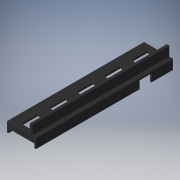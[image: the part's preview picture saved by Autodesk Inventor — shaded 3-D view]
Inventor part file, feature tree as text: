
AUTODESK INVENTOR PART (.ipt)
format: ipt  version: 2019 (Build 230136000, 136)  size: 193,024 bytes
history: native  units: mm
features: other x56, extrude x8, sketch x8
ambient origin geometry x8: Origin, YZ Plane, XZ Plane, XY Plane, X Axis, Y Axis, Z Axis, Center Point
bodies: Solid1 (feature_tree)
feature tree (72):
  extrude  "Extrusion1"  Depth=178.0mm TaperAngle=0.0deg
  extrude  "Extrusion2"  Depth=8.0mm TaperAngle=0.0deg
  extrude  "Extrusion3"  Depth=8.0mm TaperAngle=0.0deg
  extrude  "Extrusion4"  Depth=4.7mm TaperAngle=0.0deg
  extrude  "Extrusion5"  [1 undecoded]
  extrude  "Extrusion6"  [1 undecoded]
  extrude  "Extrusion7"  [1 undecoded]
  extrude  "Extrusion8"  [1 undecoded]
  other  "p_XY"
  other  "p_YZ"
  other  "p_ZX"
  other  "p_X"
  other  "p_Y"
  other  "p_Z"
  other  "p_Center"
  other  "p1_XY"
  other  "p1_YZ"
  other  "p1_ZX"
  other  "p1_X"
  other  "p1_Y"
  other  "p1_Z"
  other  "p1_Center"
  other  "p2_XY"
  other  "p2_YZ"
  other  "p2_ZX"
  other  "p2_X"
  other  "p2_Y"
  other  "p2_Z"
  other  "p2_Center"
  other  "p3_XY"
  other  "p3_YZ"
  other  "p3_ZX"
  other  "p3_X"
  other  "p3_Y"
  other  "p3_Z"
  other  "p3_Center"
  other  "p4_XY"
  other  "p4_YZ"
  other  "p4_ZX"
  other  "p4_X"
  other  "p4_Y"
  other  "p4_Z"
  other  "p4_Center"
  other  "p5_XY"
  other  "p5_YZ"
  other  "p5_ZX"
  other  "p5_X"
  other  "p5_Y"
  other  "p5_Z"
  other  "p5_Center"
  other  "p6_XY"
  other  "p6_YZ"
  other  "p6_ZX"
  other  "p6_X"
  other  "p6_Y"
  other  "p6_Z"
  other  "p6_Center"
  other  "p7_XY"
  other  "p7_YZ"
  other  "p7_ZX"
  other  "p7_X"
  other  "p7_Y"
  other  "p7_Z"
  other  "p7_Center"
  sketch  "Sketch_1"  dims[d0=178.0mm d1=0.0mm d2=8.0mm d3=0.0mm]
  sketch  "Sketch_2"  dims[d4=8.0mm d5=0.0mm d6=8.0mm d7=0.0mm]
  sketch  "Sketch_3"  dims[d8=8.0mm d9=0.0mm d10=8.0mm d11=0.0mm]
  sketch  "Sketch_4"  dims[d12=37.5mm d13=0.0mm d14=4.7mm d15=0.0mm]
  sketch  "Sketch_5"  dims[d16=0.0mm]
  sketch  "Sketch_6"
  sketch  "Sketch_10"
  sketch  "Sketch_13"
note: 4 required parameter values undecoded (feature->parameter linkage not recoverable at this tier; creation-order binding heuristic only, values carry confidence <= 0.55)
